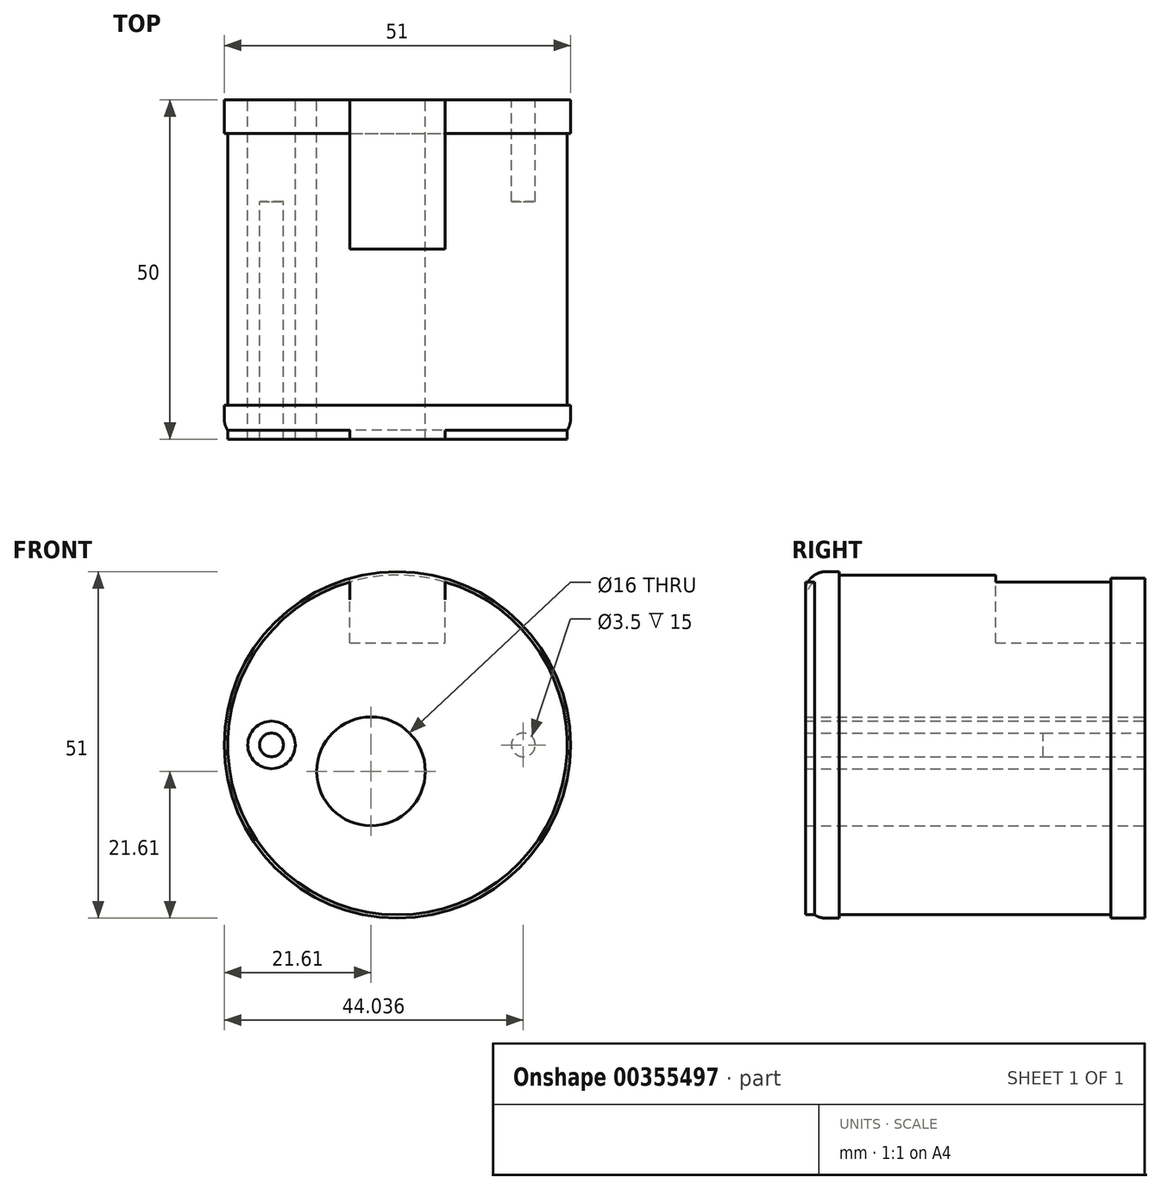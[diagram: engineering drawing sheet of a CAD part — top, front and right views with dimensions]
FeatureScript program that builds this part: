
annotation { "Feature Type Name" : "Feature", "Feature Type Description" : "" }
export const myFeature = defineFeature(function(context is Context, id is Id, definition is map)
    precondition{}
    {
        {
            var Q0;
            Q0=qCreatedBy(makeId("Front.planeOp"),FACE);
            var sketch = newSketch(context, id + "F0", { "sketchPlane" : qUnion([Q0])});
            skCircle(sketch, "E0", {"center": v(-1.61, 3.89) * mm, "radius": 25 * mm});
            skCircle(sketch, "E1.0", {"center": v(-1.61, 3.89) * mm, "radius": 25.5 * mm});
            skCircle(sketch, "E2", {"center": v(16.93, 3.9) * mm, "radius": 3.5 * mm});
            skLineSegment(sketch, "E3", {"start": v(0.16, 5.66) * mm, "end": v(16.42, 21.92) * mm});
            skPoint(sketch, "E4.start.orphan", {"position": v(-19.64, 21.92) * mm});
            skLineSegment(sketch, "E5", {"start": v(-1.61, 18.89) * mm, "end": v(-8.61, 18.89) * mm});
            skLineSegment(sketch, "E6", {"start": v(-1.61, 18.89) * mm, "end": v(5.39, 18.89) * mm});
            skCircle(sketch, "E7", {"center": v(-5.5, 0) * mm, "radius": 8 * mm});
            skCircle(sketch, "E8.MirrorC", {"center": v(-20.15, 3.9) * mm, "radius": 3.5 * mm});
            skCircle(sketch, "E9", {"center": v(16.93, 3.9) * mm, "radius": 1.75 * mm});
            skCircle(sketch, "E10", {"center": v(-20.15, 3.9) * mm, "radius": 1.75 * mm});
            skLineSegment(sketch, "E11", {"start": v(-8.61, 18.89) * mm, "end": v(-8.61, 28.4) * mm});
            skLineSegment(sketch, "E12", {"start": v(5.39, 18.89) * mm, "end": v(5.39, 28.4) * mm});
            skLineSegment(sketch, "E13", {"start": v(-1.61, 18.89) * mm, "end": v(-1.61, 29.39) * mm});
            skSolve(sketch);
        }
        {
            var Q0;
            Q0=makeQuery(id+"F0.imprint","IMPRINT",FACE,{"disambiguationData":[TD([[makeQuery(id+"F0.imprint","IMPRINT",EDGE,{"derivedFrom":sQuery(id+"F0.wireOp",EDGE,"E2")}),-1.0]])]});
            extrude(context, id + "F1", {"entities" : qUnion([Q0]), "depth" : 50 * mm});
        }
        {
            var Q0;
            Q0=makeQuery(id+"F0.imprint","IMPRINT",FACE,{"disambiguationData":[TD([[makeQuery(id+"F0.imprint","IMPRINT",EDGE,{"derivedFrom":sQuery(id+"F0.wireOp",EDGE,"E2")}),1.0]])]});
            extrude(context, id + "F2", {"entities" : qUnion([Q0]), "operationType" : NewBodyOperationType.ADD, "depth" : 50 * mm});
        }
        {
            var Q0;
            {var subQ0=sQuery(id+"F0.wireOp",EDGE,"E3");var subQ1=sQuery(id+"F0.wireOp",EDGE,"E0");var subQ2=makeQuery(id+"F0.imprint","INTERSECT",VERTEX,{"derivedFrom":[subQ1,subQ0]});Q0=makeQuery(id+"F0.imprint","IMPRINT",FACE,{"disambiguationData":[TD([[makeQuery(id+"F0.imprint","IMPRINT",EDGE,{"disambiguationData":[TD([[subQ2,1.0]])],"derivedFrom":subQ1}),-1.0]])]});}
            extrude(context, id + "F3", {"entities" : qUnion([Q0]), "operationType" : NewBodyOperationType.ADD, "depth" : 50 * mm});
        }
        {
            var Q0;
            {var subQ0=sQuery(id+"F0.wireOp",EDGE,"E3");var subQ1=sQuery(id+"F0.wireOp",EDGE,"E0");var subQ2=makeQuery(id+"F0.imprint","INTERSECT",VERTEX,{"derivedFrom":[subQ1,subQ0]});Q0=makeQuery(id+"F0.imprint","IMPRINT",FACE,{"disambiguationData":[TD([[makeQuery(id+"F0.imprint","IMPRINT",EDGE,{"disambiguationData":[TD([[subQ2,1.0]])],"derivedFrom":subQ1}),-1.0]])]});}
            extrude(context, id + "F4", {"entities" : qUnion([Q0]), "operationType" : NewBodyOperationType.REMOVE, "depth" : 45 * mm});
        }
        {
            var Q0;
            {var subQ0=sQuery(id+"F0.wireOp",EDGE,"E3");var subQ1=sQuery(id+"F0.wireOp",EDGE,"E0");var subQ2=makeQuery(id+"F0.imprint","INTERSECT",VERTEX,{"derivedFrom":[subQ1,subQ0]});Q0=makeQuery(id+"F0.imprint","IMPRINT",FACE,{"disambiguationData":[TD([[makeQuery(id+"F0.imprint","IMPRINT",EDGE,{"disambiguationData":[TD([[subQ2,-1.0]])],"derivedFrom":subQ1}),-1.0]])]});}
            extrude(context, id + "F5", {"entities" : qUnion([Q0]), "operationType" : NewBodyOperationType.ADD, "depth" : 50 * mm});
        }
        {
            var Q0;
            {var subQ0=sQuery(id+"F0.wireOp",EDGE,"E3");var subQ1=sQuery(id+"F0.wireOp",EDGE,"E0");var subQ2=makeQuery(id+"F0.imprint","INTERSECT",VERTEX,{"derivedFrom":[subQ1,subQ0]});Q0=makeQuery(id+"F0.imprint","IMPRINT",FACE,{"disambiguationData":[TD([[makeQuery(id+"F0.imprint","IMPRINT",EDGE,{"disambiguationData":[TD([[subQ2,-1.0]])],"derivedFrom":subQ1}),-1.0]])]});}
            extrude(context, id + "F6", {"entities" : qUnion([Q0]), "operationType" : NewBodyOperationType.REMOVE, "depth" : 40 * mm});
        }
        {
            var Q0;
            {var subQ0=sQuery(id+"F0.wireOp",EDGE,"5sA6tDQu-s1sJ-ZGk6-09ON-eoZIyVVLmuqZ");var subQ1=sQuery(id+"F0.wireOp",EDGE,"E0");var subQ2=makeQuery(id+"F0.imprint","INTERSECT",VERTEX,{"derivedFrom":[subQ1,subQ0]});Q0=makeQuery(id+"F0.imprint","IMPRINT",FACE,{"disambiguationData":[TD([[makeQuery(id+"F0.imprint","IMPRINT",EDGE,{"disambiguationData":[TD([[subQ2,-1.0]])],"derivedFrom":subQ1}),-1.0]])]});}
            extrude(context, id + "F7", {"entities" : qUnion([Q0]), "operationType" : NewBodyOperationType.ADD, "depth" : 50 * mm});
        }
        {
            var Q0;
            {var subQ0=sQuery(id+"F0.wireOp",EDGE,"5sA6tDQu-s1sJ-ZGk6-09ON-eoZIyVVLmuqZ");var subQ1=sQuery(id+"F0.wireOp",EDGE,"E0");var subQ2=makeQuery(id+"F0.imprint","INTERSECT",VERTEX,{"derivedFrom":[subQ1,subQ0]});Q0=makeQuery(id+"F0.imprint","IMPRINT",FACE,{"disambiguationData":[TD([[makeQuery(id+"F0.imprint","IMPRINT",EDGE,{"disambiguationData":[TD([[subQ2,-1.0]])],"derivedFrom":subQ1}),-1.0]])]});}
            extrude(context, id + "F8", {"entities" : qUnion([Q0]), "operationType" : NewBodyOperationType.REMOVE, "depth" : 45 * mm});
        }
        {
            var Q0;
            {var subQ0=sQuery(id+"F0.wireOp",EDGE,"4f877ab3-211c-4f3c-b332-6f393e1888380.MirrorCS");var subQ1=sQuery(id+"F0.wireOp",EDGE,"E0");var subQ2=makeQuery(id+"F0.imprint","INTERSECT",VERTEX,{"derivedFrom":[subQ1,subQ0]});Q0=makeQuery(id+"F0.imprint","IMPRINT",FACE,{"disambiguationData":[TD([[makeQuery(id+"F0.imprint","IMPRINT",EDGE,{"disambiguationData":[TD([[subQ2,-1.0]])],"derivedFrom":subQ1}),-1.0]])]});}
            extrude(context, id + "F9", {"entities" : qUnion([Q0]), "operationType" : NewBodyOperationType.ADD, "depth" : 50 * mm});
        }
        {
            var Q0;
            {var subQ0=sQuery(id+"F0.wireOp",EDGE,"4f877ab3-211c-4f3c-b332-6f393e1888380.MirrorCS");var subQ1=sQuery(id+"F0.wireOp",EDGE,"E0");var subQ2=makeQuery(id+"F0.imprint","INTERSECT",VERTEX,{"derivedFrom":[subQ1,subQ0]});Q0=makeQuery(id+"F0.imprint","IMPRINT",FACE,{"disambiguationData":[TD([[makeQuery(id+"F0.imprint","IMPRINT",EDGE,{"disambiguationData":[TD([[subQ2,-1.0]])],"derivedFrom":subQ1}),-1.0]])]});}
            extrude(context, id + "F10", {"entities" : qUnion([Q0]), "operationType" : NewBodyOperationType.REMOVE, "depth" : 45 * mm});
        }
        {
            var Q0;
            {var subQ0=sQuery(id+"F0.wireOp",EDGE,"E3");var subQ1=sQuery(id+"F0.wireOp",EDGE,"E0");var subQ2=makeQuery(id+"F0.imprint","INTERSECT",VERTEX,{"derivedFrom":[subQ1,subQ0]});Q0=makeQuery(id+"F0.imprint","IMPRINT",FACE,{"disambiguationData":[TD([[makeQuery(id+"F0.imprint","IMPRINT",EDGE,{"disambiguationData":[TD([[subQ2,1.0]])],"derivedFrom":subQ1}),-1.0]])]});}
            extrude(context, id + "F11", {"entities" : qUnion([Q0]), "operationType" : NewBodyOperationType.ADD, "depth" : 5 * mm});
        }
        {
            var Q0;
            {var subQ0=sQuery(id+"F0.wireOp",EDGE,"E3");var subQ1=sQuery(id+"F0.wireOp",EDGE,"E0");var subQ2=makeQuery(id+"F0.imprint","INTERSECT",VERTEX,{"derivedFrom":[subQ1,subQ0]});Q0=makeQuery(id+"F0.imprint","IMPRINT",FACE,{"disambiguationData":[TD([[makeQuery(id+"F0.imprint","IMPRINT",EDGE,{"disambiguationData":[TD([[subQ2,-1.0]])],"derivedFrom":subQ1}),-1.0]])]});}
            extrude(context, id + "F12", {"entities" : qUnion([Q0]), "operationType" : NewBodyOperationType.ADD, "depth" : 5 * mm});
        }
        {
            var Q0;
            Q0=makeQuery(id+"F0.imprint","IMPRINT",FACE,{"disambiguationData":[TD([[makeQuery(id+"F0.imprint","IMPRINT",EDGE,{"derivedFrom":sQuery(id+"F0.wireOp",EDGE,"E6")}),1.0]])]});
            extrude(context, id + "F13", {"entities" : qUnion([Q0]), "operationType" : NewBodyOperationType.ADD, "depth" : 50 * mm});
        }
        {
            var Q0;
            Q0=makeQuery(id+"F0.imprint","IMPRINT",FACE,{"disambiguationData":[TD([[makeQuery(id+"F0.imprint","IMPRINT",EDGE,{"derivedFrom":sQuery(id+"F0.wireOp",EDGE,"E5")}),-1.0]])]});
            extrude(context, id + "F14", {"entities" : qUnion([Q0]), "operationType" : NewBodyOperationType.ADD, "depth" : 50 * mm});
        }
        {
            var Q0;
            {var subQ0=sQuery(id+"F0.wireOp",EDGE,"E1.0");Q0=makeQuery(id+"F18GWe29UQfWz6s_1.boolean.opBoolean","MERGE",EDGE,{"derivedFrom":[makeQuery(id+"F5.boolean.opBoolean","MERGE",EDGE,{"derivedFrom":[makeQuery(id+"F3.opExtrude","CAP_EDGE",EDGE,{"disambiguationData":[OSD([subQ0])],"isStart":false}),makeQuery(id+"F5.opExtrude","CAP_EDGE",EDGE,{"disambiguationData":[OSD([subQ0])],"isStart":false})]}),makeQuery(id+"F18GWe29UQfWz6s_1.opExtrude","CAP_EDGE",EDGE,{"disambiguationData":[OSD([subQ0])],"isStart":false})]});}
            fillet(context, id + "F15", {"entities" : qUnion([Q0]), "radius" : 3 * mm, "tangentPropagation" : true, "allowEdgeOverflow" : false});
        }
        {
            var Q0;
            Q0=makeQuery(id+"F0.imprint","IMPRINT",FACE,{"disambiguationData":[TD([[makeQuery(id+"F0.imprint","IMPRINT",EDGE,{"derivedFrom":sQuery(id+"F0.wireOp",EDGE,"E6")}),1.0]])]});
            extrude(context, id + "F16", {"entities" : qUnion([Q0]), "operationType" : NewBodyOperationType.REMOVE, "depth" : 22 * mm});
        }
        {
            var Q0;
            Q0=makeQuery(id+"F0.imprint","IMPRINT",FACE,{"disambiguationData":[TD([[makeQuery(id+"F0.imprint","IMPRINT",EDGE,{"derivedFrom":sQuery(id+"F0.wireOp",EDGE,"E5")}),-1.0]])]});
            extrude(context, id + "F17", {"entities" : qUnion([Q0]), "operationType" : NewBodyOperationType.REMOVE, "depth" : 22 * mm});
        }
        {
            var Q0;
            Q0=makeQuery(id+"F1.opExtrude","CAP_EDGE",EDGE,{"disambiguationData":[OSD([sQuery(id+"F0.wireOp",EDGE,"E7")])],"isStart":true});
            fillet(context, id + "F18", {"entities" : qUnion([Q0]), "radius" : 1.5 * mm, "tangentPropagation" : true, "allowEdgeOverflow" : false});
        }
        {
            var Q0;
            Q0=makeQuery(id+"F1.opExtrude","CAP_EDGE",EDGE,{"disambiguationData":[OSD([sQuery(id+"F0.wireOp",EDGE,"E7")])],"isStart":false});
            fillet(context, id + "F19", {"entities" : qUnion([Q0]), "radius" : 1.5 * mm, "tangentPropagation" : true, "allowEdgeOverflow" : false});
        }
        {
            var Q0;
            Q0=makeQuery(id+"F0.imprint","IMPRINT",FACE,{"disambiguationData":[TD([[makeQuery(id+"F0.imprint","IMPRINT",EDGE,{"derivedFrom":sQuery(id+"F0.wireOp",EDGE,"E8.MirrorC")}),-1.0]])]});
            extrude(context, id + "F20", {"entities" : qUnion([Q0]), "operationType" : NewBodyOperationType.ADD, "depth" : 50 * mm});
        }
        {
            var Q0;
            Q0=makeQuery(id+"F0.imprint","IMPRINT",FACE,{"disambiguationData":[TD([[makeQuery(id+"F0.imprint","IMPRINT",EDGE,{"derivedFrom":sQuery(id+"F0.wireOp",EDGE,"E10")}),1.0]])]});
            extrude(context, id + "F21", {"entities" : qUnion([Q0]), "operationType" : NewBodyOperationType.ADD, "depth" : 50 * mm});
        }
        {
            var Q0;
            Q0=makeQuery(id+"F0.imprint","IMPRINT",FACE,{"disambiguationData":[TD([[makeQuery(id+"F0.imprint","IMPRINT",EDGE,{"derivedFrom":sQuery(id+"F0.wireOp",EDGE,"E9")}),1.0]])]});
            extrude(context, id + "F22", {"entities" : qUnion([Q0]), "operationType" : NewBodyOperationType.ADD, "depth" : 50 * mm});
        }
        {
            var Q0;
            Q0=makeQuery(id+"F0.imprint","IMPRINT",FACE,{"disambiguationData":[TD([[makeQuery(id+"F0.imprint","IMPRINT",EDGE,{"derivedFrom":sQuery(id+"F0.wireOp",EDGE,"E9")}),1.0]])]});
            extrude(context, id + "F23", {"entities" : qUnion([Q0]), "operationType" : NewBodyOperationType.REMOVE, "depth" : 15 * mm});
        }
        {
            var Q0;
            Q0=makeQuery(id+"F0.imprint","IMPRINT",FACE,{"disambiguationData":[TD([[makeQuery(id+"F0.imprint","IMPRINT",EDGE,{"derivedFrom":sQuery(id+"F0.wireOp",EDGE,"E10")}),1.0]])]});
            extrude(context, id + "F24", {"entities" : qUnion([Q0]), "operationType" : NewBodyOperationType.REMOVE, "depth" : 15 * mm});
        }
    });
